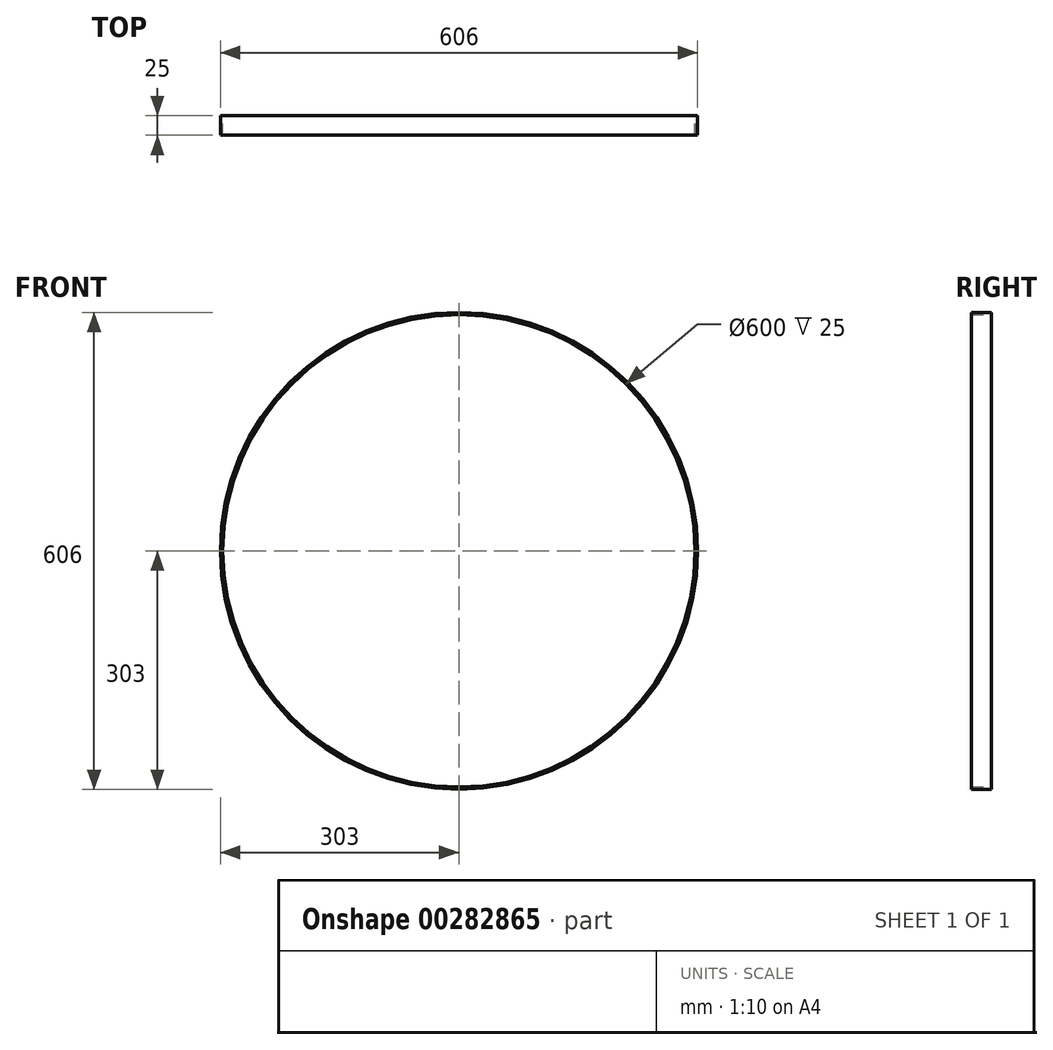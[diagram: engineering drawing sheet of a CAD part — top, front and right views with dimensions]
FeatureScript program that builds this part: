
annotation { "Feature Type Name" : "Feature", "Feature Type Description" : "" }
export const myFeature = defineFeature(function(context is Context, id is Id, definition is map)
    precondition{}
    {
        {
            var Q0;
            Q0=qCreatedBy(makeId("Front.planeOp"),FACE);
            var sketch = newSketch(context, id + "F0", { "sketchPlane" : qUnion([Q0])});
            skCircle(sketch, "E0", {"center": v(0, 0) * mm, "radius": 300 * mm});
            skCircle(sketch, "E1", {"center": v(0, 0) * mm, "radius": 303 * mm});
            skCircle(sketch, "E2", {"center": v(0, -251) * mm, "radius": 49 * mm});
            skCircle(sketch, "E3", {"center": v(-84.5, -352) * mm, "radius": 59 * mm});
            skCircle(sketch, "E4", {"center": v(84.5, -352) * mm, "radius": 59 * mm});
            skLineSegment(sketch, "E5", {"start": v(0, 0) * mm, "end": v(0, -352) * mm, "construction": true});
            skLineSegment(sketch, "E6", {"start": v(84.5, -352) * mm, "end": v(0, -352) * mm, "construction": true});
            skLineSegment(sketch, "E7", {"start": v(-84.5, -352) * mm, "end": v(0, -352) * mm, "construction": true});
            skCircle(sketch, "E8", {"center": v(0, -241) * mm, "radius": 49 * mm, "construction": true});
            skLineSegment(sketch, "E9.bottom", {"start": v(-163.63, -290) * mm, "end": v(163.63, -290) * mm, "construction": true});
            skLineSegment(sketch, "E9.top", {"start": v(-163.63, -293) * mm, "end": v(163.63, -293) * mm, "construction": true});
            skLineSegment(sketch, "E9.left", {"start": v(-163.63, -290) * mm, "end": v(-163.63, -293) * mm});
            skLineSegment(sketch, "E9.right", {"start": v(163.63, -290) * mm, "end": v(163.63, -293) * mm});
            skPoint(sketch, "E9.middle", {"position": v(0, -291.5) * mm});
            skSolve(sketch);
        }
        {
            var Q0;
            Q0=makeQuery(id+"F0.imprint","IMPRINT",FACE,{"disambiguationData":[TD([[makeQuery(id+"F0.imprint","IMPRINT",EDGE,{"derivedFrom":sQuery(id+"F0.wireOp",EDGE,"E0")}),-1.0]])]});
            extrude(context, id + "F1", {"entities" : qUnion([Q0]), "depth" : 25 * mm});
        }
    });
